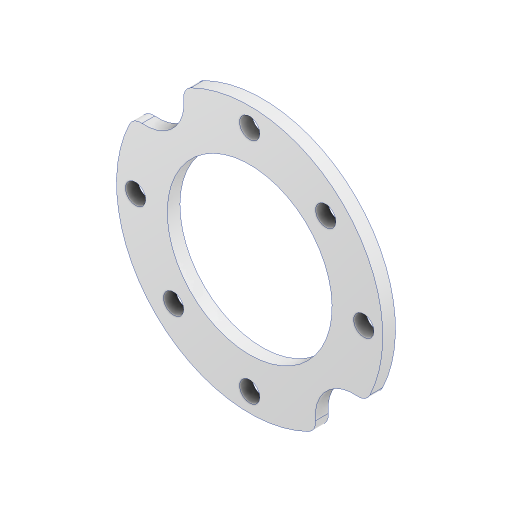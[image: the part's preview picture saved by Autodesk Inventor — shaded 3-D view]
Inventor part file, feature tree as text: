
AUTODESK INVENTOR PART (.ipt)
format: ipt  version: 2023 (Build 270158000, 158)  size: 281,600 bytes
history: native  units: mm
features: other x5, extrude x2, sketch x2, fillet x1, reference x1, projected_geometry x1
ambient origin geometry x8: Origin, YZ Plane, XZ Plane, XY Plane, X Axis, Y Axis, Z Axis, Center Point
bodies: Body1 (feature_tree)
feature tree (12):
  other  "솔리드1"
  other  "작업 평면1"
  extrude  "돌출1"  Depth=42.0mm
  fillet  "모깎기1"  Radius=1.0mm
  extrude  "돌출2"  Depth=2.0mm
  sketch  "스케치1"
  reference  "참조1"
  sketch  "스케치2"
  projected_geometry  "투영된 루프1"
  other  "<userpath>\Desktop\2022 manipulator (국방로봇)\JWM.iam"
  other  "JWM.iam"
  other  "기어2:6"
